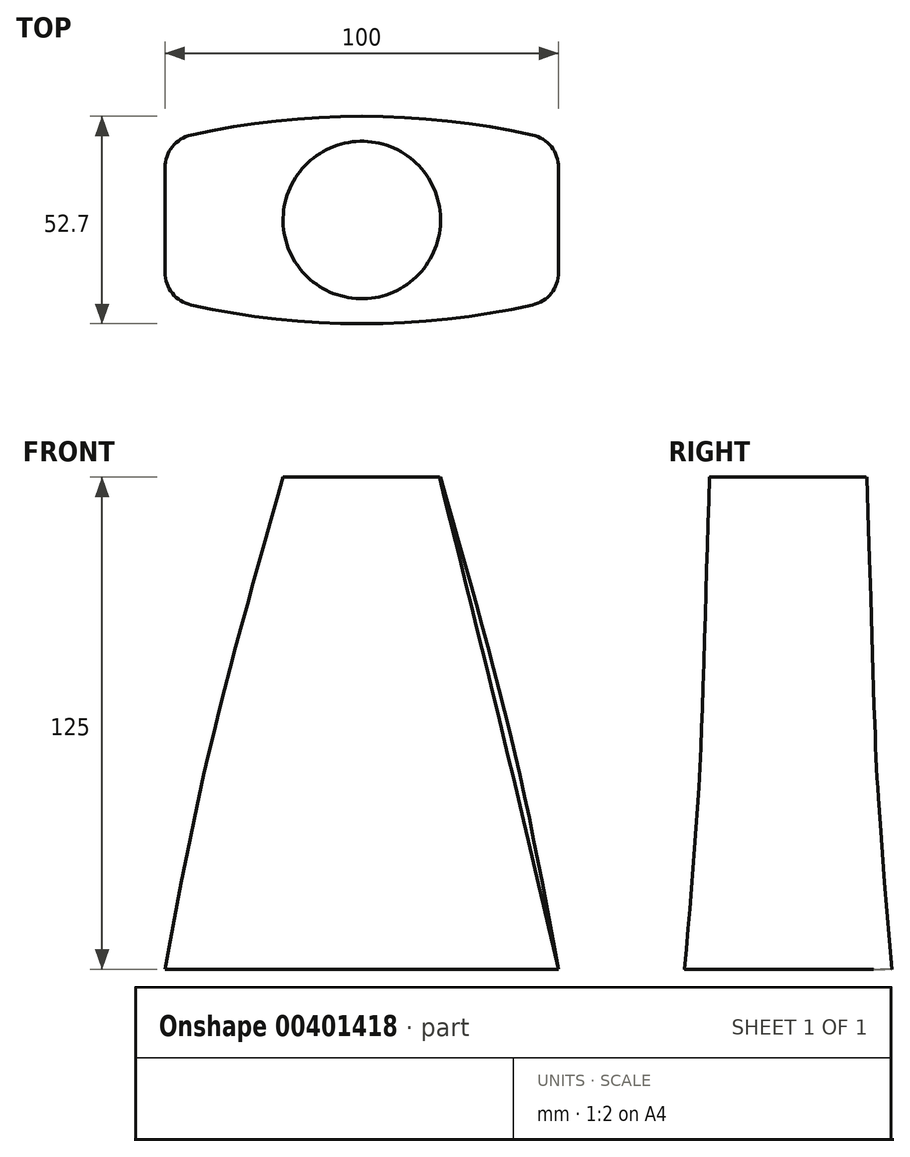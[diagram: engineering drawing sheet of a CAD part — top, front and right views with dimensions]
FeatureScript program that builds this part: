
annotation { "Feature Type Name" : "Feature", "Feature Type Description" : "" }
export const myFeature = defineFeature(function(context is Context, id is Id, definition is map)
    precondition{}
    {
        {
            var Q0;
            Q0=qCreatedBy(makeId("Top.planeOp"),FACE);
            var sketch = newSketch(context, id + "F0", { "sketchPlane" : qUnion([Q0])});
            skLineSegment(sketch, "E0.bottom", {"start": v(50, -20) * mm, "end": v(-50, -20) * mm, "construction": true});
            skLineSegment(sketch, "E0.top", {"start": v(50, 20) * mm, "end": v(-50, 20) * mm, "construction": true});
            skLineSegment(sketch, "E0.left", {"start": v(50, -13.3) * mm, "end": v(50, 13.3) * mm});
            skLineSegment(sketch, "E0.right", {"start": v(-50, -13.3) * mm, "end": v(-50, 13.3) * mm});
            skPoint(sketch, "E0.middle", {"position": v(0, 0) * mm});
            skArc(sketch, "E1", {"start": v(43.34, 21.6) * mm, "mid": v(0, 26.35) * mm, "end": v(-43.34, 21.6) * mm});
            skArc(sketch, "E2", {"start": v(-43.34, -21.6) * mm, "mid": v(0, -26.35) * mm, "end": v(43.34, -21.6) * mm});
            skPoint(sketch, "E3.visualSharp", {"position": v(-50, 20) * mm});
            skArc(sketch, "E3.filletArc", {"start": v(-43.34, 21.6) * mm, "mid": v(-48.13, 18.62) * mm, "end": v(-50, 13.3) * mm});
            skPoint(sketch, "E4.visualSharp", {"position": v(50, 20) * mm});
            skArc(sketch, "E4.filletArc", {"start": v(50, 13.3) * mm, "mid": v(48.13, 18.62) * mm, "end": v(43.34, 21.6) * mm});
            skPoint(sketch, "E5.visualSharp", {"position": v(50, -20) * mm});
            skArc(sketch, "E5.filletArc", {"start": v(43.34, -21.6) * mm, "mid": v(48.13, -18.62) * mm, "end": v(50, -13.3) * mm});
            skPoint(sketch, "E6.visualSharp", {"position": v(-50, -20) * mm});
            skArc(sketch, "E6.filletArc", {"start": v(-50, -13.3) * mm, "mid": v(-48.13, -18.62) * mm, "end": v(-43.34, -21.6) * mm});
            skSolve(sketch);
        }
        {
            var Q0;
            Q0=qCreatedBy(makeId("Top.planeOp"),FACE);
            cPlane(context, id + "F1", {"entities" : qUnion([Q0]), "cplaneType" : CPlaneType.OFFSET, "offset" : 50 * mm, "width" : 150 * mm, "height" : 150 * mm});
        }
        {
            var Q0;
            Q0=qCreatedBy(id+"F1.planeOp",FACE);
            var sketch = newSketch(context, id + "F2", { "sketchPlane" : qUnion([Q0])});
            skEllipse(sketch, "E7", {"center": v(0, 0) * mm, "majorRadius": 40 * mm, "minorRadius": 22.5 * mm, "majorAxis": v(-1, 0)});
            skSolve(sketch);
        }
        {
            var Q0;
            Q0=qCreatedBy(makeId("Top.planeOp"),FACE);
            cPlane(context, id + "F3", {"entities" : qUnion([Q0]), "cplaneType" : CPlaneType.OFFSET, "offset" : 125 * mm, "width" : 150 * mm, "height" : 150 * mm});
        }
        {
            var Q0;
            Q0=qCreatedBy(id+"F3.planeOp",FACE);
            var sketch = newSketch(context, id + "F4", { "sketchPlane" : qUnion([Q0])});
            skCircle(sketch, "E8", {"center": v(0, 0) * mm, "radius": 20 * mm});
            skSolve(sketch);
        }
        {
            var Q0;
            Q0=makeQuery(id+"F0.imprint","IMPRINT",FACE,{"disambiguationData":[TD([[makeQuery(id+"F0.imprint","IMPRINT",EDGE,{"derivedFrom":sQuery(id+"F0.wireOp",EDGE,"E0.left")}),1.0]])]});
            var Q1;
            Q1=makeQuery(id+"F2.imprint","IMPRINT",FACE,{"disambiguationData":[TD([[makeQuery(id+"F2.imprint","IMPRINT",EDGE,{"derivedFrom":sQuery(id+"F2.wireOp",EDGE,"E7")}),1.0]])]});
            var Q2;
            Q2=makeQuery(id+"F4.imprint","IMPRINT",FACE,{"disambiguationData":[TD([[makeQuery(id+"F4.imprint","IMPRINT",EDGE,{"derivedFrom":sQuery(id+"F4.wireOp",EDGE,"E8")}),1.0]])]});
            loft(context, id + "F5", {"sheetProfilesArray" : [{ "sheetProfileEntities" : qUnion([Q0]) }, { "sheetProfileEntities" : qUnion([Q1]) }, { "sheetProfileEntities" : qUnion([Q2]) }]});
        }
    });
